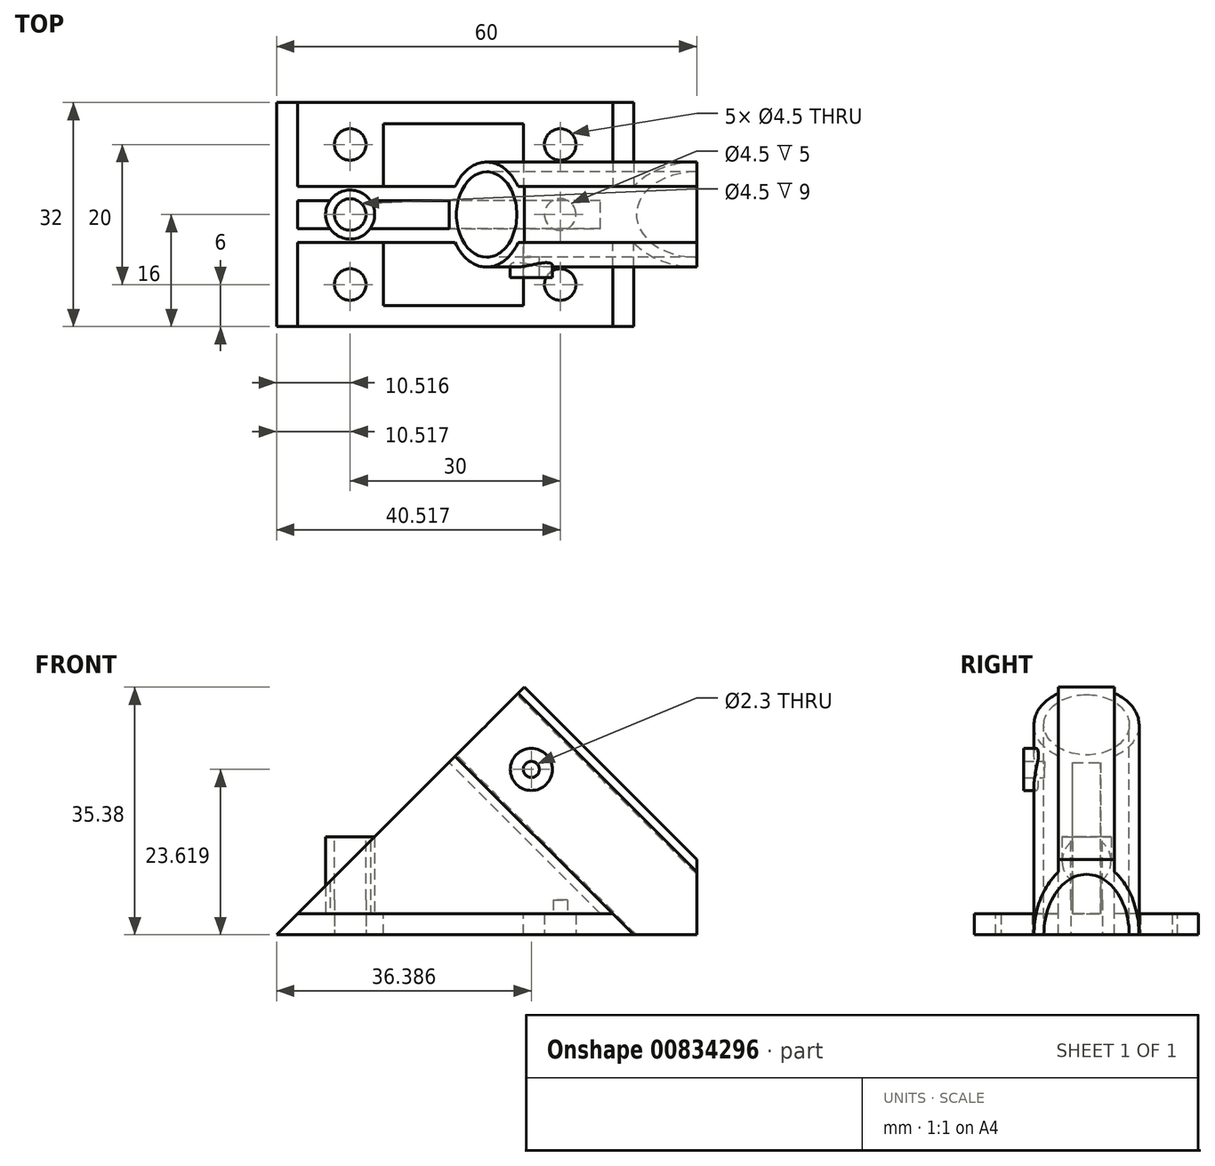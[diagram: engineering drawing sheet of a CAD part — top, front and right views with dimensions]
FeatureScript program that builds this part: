
annotation { "Feature Type Name" : "Feature", "Feature Type Description" : "" }
export const myFeature = defineFeature(function(context is Context, id is Id, definition is map)
    precondition{}
    {
        {
            var Q0;
            Q0=qCreatedBy(makeId("Front.planeOp"),FACE);
            var sketch = newSketch(context, id + "F0", { "sketchPlane" : qUnion([Q0])});
            skLineSegment(sketch, "E0", {"start": v(0, 0) * mm, "end": v(60, 0) * mm});
            skLineSegment(sketch, "E1", {"start": v(60, 0) * mm, "end": v(60, 60) * mm});
            skLineSegment(sketch, "E2", {"start": v(60, 60) * mm, "end": v(0, 0) * mm});
            skSolve(sketch);
        }
        {
            var Q0;
            Q0=makeQuery(id+"F0.imprint","IMPRINT",FACE,{"disambiguationData":[TD([[makeQuery(id+"F0.imprint","IMPRINT",EDGE,{"derivedFrom":sQuery(id+"F0.wireOp",EDGE,"E0")}),1.0]])]});
            extrude(context, id + "F1", {"entities" : qUnion([Q0]), "depth" : 60 * mm, "offsetDistance" : 25 * mm});
        }
        {
            var Q0;
            Q0=makeQuery(id+"F1.opExtrude","SWEPT_FACE",FACE,{"disambiguationData":[OSD([sQuery(id+"F0.wireOp",EDGE,"E2")])]});
            var sketch = newSketch(context, id + "F2", { "sketchPlane" : qUnion([Q0])});
            skLineSegment(sketch, "E3", {"start": v(0, 0) * mm, "end": v(26, 0) * mm});
            skLineSegment(sketch, "E4", {"start": v(26, 0) * mm, "end": v(26, 36.09) * mm});
            skArc(sketch, "E5", {"start": v(26, 48.77) * mm, "mid": v(22.5, 42.43) * mm, "end": v(26, 36.09) * mm});
            skLineSegment(sketch, "E6", {"start": v(26, 36.09) * mm, "end": v(26, 48.77) * mm, "construction": true});
            skLineSegment(sketch, "E7", {"start": v(26, 48.77) * mm, "end": v(26, 84.85) * mm});
            skLineSegment(sketch, "E8", {"start": v(26, 84.85) * mm, "end": v(0, 84.85) * mm});
            skLineSegment(sketch, "E9", {"start": v(0, 84.85) * mm, "end": v(0, 0) * mm});
            skLineSegment(sketch, "E10", {"start": v(34, 48.77) * mm, "end": v(34, 84.85) * mm});
            skLineSegment(sketch, "E11", {"start": v(34, 84.85) * mm, "end": v(60, 84.85) * mm});
            skLineSegment(sketch, "E12", {"start": v(60, 84.85) * mm, "end": v(60, 0) * mm});
            skLineSegment(sketch, "E13", {"start": v(60, 0) * mm, "end": v(34, 0) * mm});
            skLineSegment(sketch, "E14", {"start": v(34, 0) * mm, "end": v(34, 36.09) * mm});
            skArc(sketch, "E15", {"start": v(34, 36.09) * mm, "mid": v(37.5, 42.43) * mm, "end": v(34, 48.77) * mm});
            skLineSegment(sketch, "E16", {"start": v(34, 36.09) * mm, "end": v(34, 48.77) * mm, "construction": true});
            skLineSegment(sketch, "E17", {"start": v(30, 42.43) * mm, "end": v(60, 42.43) * mm, "construction": true});
            skLineSegment(sketch, "E18", {"start": v(30, 42.43) * mm, "end": v(0, 42.43) * mm, "construction": true});
            skSolve(sketch);
        }
        {
            var Q0;
            Q0=qSketchRegion(id+"F2",true);
            extrude(context, id + "F3", {"entities" : qUnion([Q0]), "operationType" : NewBodyOperationType.REMOVE, "endBound" : BoundingType.UP_TO_NEXT, "oppositeDirection" : true, "depth" : 25 * mm, "offsetDistance" : 25 * mm});
        }
        {
            var Q0;
            Q0=makeQuery(id+"F3.boolean.opBoolean","COPY",FACE,{"derivedFrom":makeQuery(id+"F3.opExtrude","SWEPT_FACE",FACE,{"disambiguationData":[OSD([sQuery(id+"F2.wireOp",EDGE,"E14")])]})});
            var sketch = newSketch(context, id + "F4", { "sketchPlane" : qUnion([Q0])});
            skCircle(sketch, "E19", {"center": v(36.39, 23.62) * mm, "radius": 3 * mm});
            skLineSegment(sketch, "E20", {"start": v(36.39, 23.62) * mm, "end": v(40.87, 28.1) * mm, "construction": true});
            skLineSegment(sketch, "E21", {"start": v(36.39, 23.62) * mm, "end": v(31.9, 19.13) * mm, "construction": true});
            skSolve(sketch);
        }
        {
            var Q0;
            Q0=qSketchRegion(id+"F4",true);
            extrude(context, id + "F5", {"entities" : qUnion([Q0]), "operationType" : NewBodyOperationType.ADD, "depth" : 5 * mm, "offsetDistance" : 25 * mm});
        }
        {
            var Q0;
            Q0=makeQuery(id+"F1.opExtrude","SWEPT_FACE",FACE,{"disambiguationData":[OSD([sQuery(id+"F0.wireOp",EDGE,"E2")])]});
            var sketch = newSketch(context, id + "F6", { "sketchPlane" : qUnion([Q0])});
            skCircle(sketch, "E22", {"center": v(30, 42.43) * mm, "radius": 6.1 * mm});
            skSolve(sketch);
        }
        {
            var Q0;
            Q0=qSketchRegion(id+"F6",true);
            extrude(context, id + "F7", {"entities" : qUnion([Q0]), "operationType" : NewBodyOperationType.REMOVE, "endBound" : BoundingType.UP_TO_NEXT, "oppositeDirection" : true, "depth" : 25 * mm, "offsetDistance" : 25 * mm});
        }
        {
            var Q0;
            {var subQ0=sQuery(id+"F10.wireOp",EDGE,"E30");Q0=makeQuery(id+"F12.boolean.opBoolean","MERGE",FACE,{"derivedFrom":[makeQuery(id+"F11.boolean.opBoolean","MERGE",FACE,{"derivedFrom":[makeQuery(id+"F1.opExtrude","SWEPT_FACE",FACE,{"disambiguationData":[OSD([sQuery(id+"F0.wireOp",EDGE,"E2")])]}),makeQuery(id+"F11.opExtrude","SWEPT_FACE",FACE,{"disambiguationData":[OSD([subQ0])]})]}),makeQuery(id+"F12.opExtrude","SWEPT_FACE",FACE,{"disambiguationData":[OSD([subQ0])]})]});}
            var sketch = newSketch(context, id + "F8", { "sketchPlane" : qUnion([Q0])});
            skLineSegment(sketch, "E23", {"start": v(28, 34.83) * mm, "end": v(28, 4.24) * mm});
            skLineSegment(sketch, "E24", {"start": v(28, 4.24) * mm, "end": v(32, 4.24) * mm});
            skLineSegment(sketch, "E25", {"start": v(32, 4.24) * mm, "end": v(32, 34.83) * mm});
            skLineSegment(sketch, "E26", {"start": v(32, 34.83) * mm, "end": v(28, 34.83) * mm});
            skLineSegment(sketch, "E27", {"start": v(26, 4.24) * mm, "end": v(28, 4.24) * mm, "construction": true});
            skLineSegment(sketch, "E28", {"start": v(34, 4.24) * mm, "end": v(32, 4.24) * mm, "construction": true});
            skLineSegment(sketch, "E29.bottom", {"start": v(26, 84.85) * mm, "end": v(34, 84.85) * mm});
            skLineSegment(sketch, "E29.top", {"start": v(26, 50.03) * mm, "end": v(34, 50.03) * mm});
            skLineSegment(sketch, "E29.left", {"start": v(26, 84.85) * mm, "end": v(26, 50.03) * mm});
            skLineSegment(sketch, "E29.right", {"start": v(34, 84.85) * mm, "end": v(34, 50.03) * mm});
            skSolve(sketch);
        }
        {
            var Q0;
            Q0=qSketchRegion(id+"F8",true);
            extrude(context, id + "F9", {"entities" : qUnion([Q0]), "operationType" : NewBodyOperationType.REMOVE, "endBound" : BoundingType.UP_TO_NEXT, "oppositeDirection" : true, "depth" : 25 * mm, "offsetDistance" : 25 * mm});
        }
        {
            var Q0;
            Q0=makeQuery(id+"F3.boolean.opBoolean","COPY",FACE,{"derivedFrom":makeQuery(id+"F3.opExtrude","SWEPT_FACE",FACE,{"disambiguationData":[OSD([sQuery(id+"F2.wireOp",EDGE,"E14")])]})});
            var sketch = newSketch(context, id + "F10", { "sketchPlane" : qUnion([Q0])});
            skLineSegment(sketch, "E30", {"start": v(0, 0) * mm, "end": v(3, 3) * mm});
            skLineSegment(sketch, "E31", {"start": v(3, 3) * mm, "end": v(48.03, 3) * mm});
            skLineSegment(sketch, "E32", {"start": v(48.03, 3) * mm, "end": v(51.03, 0) * mm});
            skLineSegment(sketch, "E33", {"start": v(51.03, 0) * mm, "end": v(0, 0) * mm});
            skSolve(sketch);
        }
        {
            var Q0;
            Q0=qSketchRegion(id+"F10",true);
            extrude(context, id + "F11", {"entities" : qUnion([Q0]), "operationType" : NewBodyOperationType.ADD, "depth" : 12 * mm, "offsetDistance" : 25 * mm});
        }
        {
            var Q0;
            Q0=qSketchRegion(id+"F10",true);
            extrude(context, id + "F12", {"entities" : qUnion([Q0]), "operationType" : NewBodyOperationType.ADD, "oppositeDirection" : true, "depth" : 20 * mm, "offsetDistance" : 25 * mm});
        }
        {
            var Q0;
            {var subQ0=sQuery(id+"F10.wireOp",EDGE,"E33");Q0=makeQuery(id+"F12.boolean.opBoolean","MERGE",FACE,{"derivedFrom":[makeQuery(id+"F11.boolean.opBoolean","MERGE",FACE,{"derivedFrom":[makeQuery(id+"F1.opExtrude","SWEPT_FACE",FACE,{"disambiguationData":[OSD([sQuery(id+"F0.wireOp",EDGE,"E0")])]}),makeQuery(id+"F11.opExtrude","SWEPT_FACE",FACE,{"disambiguationData":[OSD([subQ0])]})]}),makeQuery(id+"F12.opExtrude","SWEPT_FACE",FACE,{"disambiguationData":[OSD([subQ0])]})]});}
            var sketch = newSketch(context, id + "F13", { "sketchPlane" : qUnion([Q0])});
            skCircle(sketch, "E34", {"center": v(10.52, 40) * mm, "radius": 2.25 * mm});
            skCircle(sketch, "E35", {"center": v(40.52, 40) * mm, "radius": 2.25 * mm});
            skCircle(sketch, "E36", {"center": v(40.52, 20) * mm, "radius": 2.25 * mm});
            skCircle(sketch, "E37", {"center": v(10.52, 20) * mm, "radius": 2.25 * mm});
            skLineSegment(sketch, "E38", {"start": v(10.52, 40) * mm, "end": v(40.52, 40) * mm, "construction": true});
            skLineSegment(sketch, "E39", {"start": v(40.52, 40) * mm, "end": v(40.52, 20) * mm, "construction": true});
            skLineSegment(sketch, "E40", {"start": v(10.52, 20) * mm, "end": v(40.52, 20) * mm, "construction": true});
            skLineSegment(sketch, "E41", {"start": v(10.52, 40) * mm, "end": v(10.52, 20) * mm, "construction": true});
            skLineSegment(sketch, "E42", {"start": v(40.52, 40) * mm, "end": v(51.03, 40) * mm, "construction": true});
            skLineSegment(sketch, "E43", {"start": v(10.52, 40) * mm, "end": v(10.52, 46) * mm, "construction": true});
            skLineSegment(sketch, "E44", {"start": v(10.52, 20) * mm, "end": v(0, 20) * mm, "construction": true});
            skLineSegment(sketch, "E45", {"start": v(40.52, 20) * mm, "end": v(40.52, 14) * mm, "construction": true});
            skSolve(sketch);
        }
        {
            var Q0;
            Q0=qSketchRegion(id+"F13",true);
            extrude(context, id + "F14", {"entities" : qUnion([Q0]), "operationType" : NewBodyOperationType.REMOVE, "endBound" : BoundingType.UP_TO_NEXT, "oppositeDirection" : true, "depth" : 25 * mm, "offsetDistance" : 25 * mm});
        }
        {
            var Q0;
            Q0=makeQuery(id+"F11.opExtrude","SWEPT_FACE",FACE,{"disambiguationData":[OSD([sQuery(id+"F10.wireOp",EDGE,"E31")])]});
            var sketch = newSketch(context, id + "F15", { "sketchPlane" : qUnion([Q0])});
            skLineSegment(sketch, "E46.bottom", {"start": v(35.27, -17) * mm, "end": v(15.27, -17) * mm});
            skLineSegment(sketch, "E46.top", {"start": v(35.27, -26) * mm, "end": v(15.27, -26) * mm});
            skLineSegment(sketch, "E46.left", {"start": v(35.27, -17) * mm, "end": v(35.27, -26) * mm});
            skLineSegment(sketch, "E46.right", {"start": v(15.27, -17) * mm, "end": v(15.27, -26) * mm});
            skLineSegment(sketch, "E47.bottom", {"start": v(35.27, -34) * mm, "end": v(15.27, -34) * mm});
            skLineSegment(sketch, "E47.top", {"start": v(35.27, -43) * mm, "end": v(15.27, -43) * mm});
            skLineSegment(sketch, "E47.left", {"start": v(35.27, -34) * mm, "end": v(35.27, -43) * mm});
            skLineSegment(sketch, "E47.right", {"start": v(15.27, -34) * mm, "end": v(15.27, -43) * mm});
            skSolve(sketch);
        }
        {
            var Q0;
            Q0=qSketchRegion(id+"F15",true);
            extrude(context, id + "F16", {"entities" : qUnion([Q0]), "operationType" : NewBodyOperationType.REMOVE, "endBound" : BoundingType.UP_TO_NEXT, "oppositeDirection" : true, "depth" : 25 * mm, "offsetDistance" : 25 * mm});
        }
        {
            var Q0;
            Q0=makeQuery(id+"F16.boolean.opBoolean","MERGE",FACE,{"derivedFrom":[makeQuery(id+"F3.boolean.opBoolean","COPY",FACE,{"derivedFrom":makeQuery(id+"F3.opExtrude","SWEPT_FACE",FACE,{"disambiguationData":[OSD([sQuery(id+"F2.wireOp",EDGE,"E14")])]})})],"fromTools":[makeQuery(id+"F16.opExtrude","SWEPT_FACE",FACE,{"disambiguationData":[OSD([sQuery(id+"F15.wireOp",EDGE,"E47.bottom")])]})]});
            var sketch = newSketch(context, id + "F17", { "sketchPlane" : qUnion([Q0])});
            skCircle(sketch, "E48", {"center": v(36.39, 23.62) * mm, "radius": 1.15 * mm});
            skLineSegment(sketch, "E49", {"start": v(36.39, 23.62) * mm, "end": v(40.87, 28.1) * mm, "construction": true});
            skLineSegment(sketch, "E50", {"start": v(36.39, 23.62) * mm, "end": v(31.9, 19.13) * mm, "construction": true});
            skLineSegment(sketch, "E51", {"start": v(36.39, 23.62) * mm, "end": v(36.39, 3) * mm, "construction": true});
            skSolve(sketch);
        }
        {
            var Q0;
            Q0=qSketchRegion(id+"F17",true);
            extrude(context, id + "F18", {"entities" : qUnion([Q0]), "operationType" : NewBodyOperationType.REMOVE, "depth" : 25 * mm, "offsetDistance" : 25 * mm});
        }
        {
            var Q0;
            Q0=makeQuery(id+"F12.boolean.opBoolean","SPLIT",FACE,{"disambiguationData":[TD([makeQuery(id+"F9.boolean.opBoolean","COPY",FACE,{"derivedFrom":makeQuery(id+"F9.opExtrude","SWEPT_FACE",FACE,{"disambiguationData":[OSD([sQuery(id+"F8.wireOp",EDGE,"E23")])]})})])],"derivedFrom":makeQuery(id+"F12.opExtrude","SWEPT_FACE",FACE,{"disambiguationData":[OSD([sQuery(id+"F10.wireOp",EDGE,"E31")])]})});
            var sketch = newSketch(context, id + "F19", { "sketchPlane" : qUnion([Q0])});
            skCircle(sketch, "E52", {"center": v(10.52, -30) * mm, "radius": 3.5 * mm});
            skLineSegment(sketch, "E53", {"start": v(10.52, -30) * mm, "end": v(10.52, -14) * mm, "construction": true});
            skLineSegment(sketch, "E54", {"start": v(10.52, -30) * mm, "end": v(10.52, -46) * mm, "construction": true});
            skSolve(sketch);
        }
        {
            var Q0;
            Q0 = qSketchRegion(id + "F19", true);
            extrude(context, id + "F20", {"entities" : qUnion([Q0]), "operationType" : NewBodyOperationType.ADD, "depth" : 11 * mm, "offsetDistance" : 25 * mm});
        }
        {
            var Q0;
            {var subQ0=sQuery(id+"F10.wireOp",EDGE,"E33");Q0=makeQuery(id+"F12.boolean.opBoolean","MERGE",FACE,{"derivedFrom":[makeQuery(id+"F11.boolean.opBoolean","MERGE",FACE,{"derivedFrom":[makeQuery(id+"F1.opExtrude","SWEPT_FACE",FACE,{"disambiguationData":[OSD([sQuery(id+"F0.wireOp",EDGE,"E0")])]}),makeQuery(id+"F11.opExtrude","SWEPT_FACE",FACE,{"disambiguationData":[OSD([subQ0])]})]}),makeQuery(id+"F12.opExtrude","SWEPT_FACE",FACE,{"disambiguationData":[OSD([subQ0])]})]});}
            var sketch = newSketch(context, id + "F21", { "sketchPlane" : qUnion([Q0])});
            skCircle(sketch, "E55", {"center": v(10.52, 30) * mm, "radius": 2.25 * mm});
            skCircle(sketch, "E56", {"center": v(40.52, 30) * mm, "radius": 2.25 * mm});
            skLineSegment(sketch, "E57", {"start": v(40.52, 30) * mm, "end": v(10.52, 30) * mm, "construction": true});
            skLineSegment(sketch, "E58", {"start": v(40.52, 30) * mm, "end": v(40.52, 14) * mm, "construction": true});
            skLineSegment(sketch, "E59", {"start": v(40.52, 30) * mm, "end": v(40.52, 46) * mm, "construction": true});
            skLineSegment(sketch, "E60", {"start": v(10.52, 30) * mm, "end": v(0, 30) * mm, "construction": true});
            skLineSegment(sketch, "E61", {"start": v(40.52, 30) * mm, "end": v(51.03, 30) * mm, "construction": true});
            skPoint(sketch, "E61.endSnap0", {"position": v(51.38, 30) * mm});
            skLineSegment(sketch, "E62", {"start": v(51.03, 26) * mm, "end": v(51.03, 34) * mm, "construction": true});
            skSolve(sketch);
        }
        {
            var Q0;
            Q0 = qSketchRegion(id + "F21", true);
            extrude(context, id + "F22", {"entities" : qUnion([Q0]), "operationType" : NewBodyOperationType.REMOVE, "oppositeDirection" : true, "depth" : 5 * mm, "offsetDistance" : 25 * mm});
        }
        {
            var Q0;
            Q0=makeQuery(id+"F20.opExtrude","CAP_FACE",FACE,{"disambiguationData":[OSD([sQuery(id+"F19.wireOp",EDGE,"E52")])],"isStart":false});
            var sketch = newSketch(context, id + "F23", { "sketchPlane" : qUnion([Q0])});
            skCircle(sketch, "E63", {"center": v(10.52, -30) * mm, "radius": 2.25 * mm});
            skSolve(sketch);
        }
        {
            var Q0;
            Q0=makeQuery(id+"F23.imprint","IMPRINT",FACE,{"disambiguationData":[TD([[makeQuery(id+"F23.imprint","IMPRINT",EDGE,{"derivedFrom":sQuery(id+"F23.wireOp",EDGE,"E63")}),1.0]])]});
            var Q1;
            Q1=sQuery(id+"F23.wireOp",EDGE,"E63");
            extrude(context, id + "F24", {"entities" : qUnion([Q0]), "operationType" : NewBodyOperationType.REMOVE, "surfaceEntities" : qUnion([Q1]), "endBound" : BoundingType.THROUGH_ALL, "oppositeDirection" : true, "depth" : 25 * mm, "offsetDistance" : 25 * mm});
        }
    });
